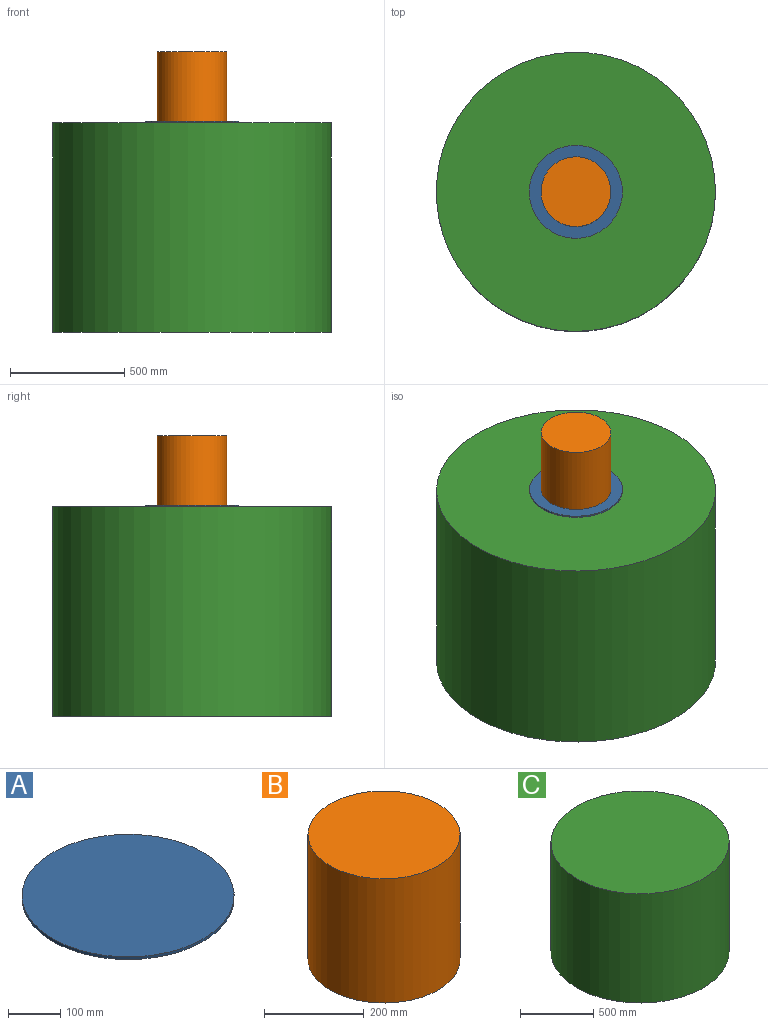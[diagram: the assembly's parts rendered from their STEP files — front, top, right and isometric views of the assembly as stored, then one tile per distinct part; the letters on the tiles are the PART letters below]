
ASSEMBLY  parts=3 mates=2
PART A: 3 faces, bbox 406.4x406.4x6.4 mm
  f0: cylinder r=203.2mm len=406.4mm, axis (0,0,-1), area 8107.3mm2, adj f1,f2
  f1: plane 406.4x406.4mm, normal (0,0,1), area 129717.1mm2, adj f0
  f2: plane 406.4x406.4mm, normal (0,0,-1), area 129717.1mm2, adj f0
PART B: 3 faces, bbox 304.8x304.8x304.8 mm
  f0: cylinder r=152.4mm len=304.8mm, axis (0,0,-1), area 291863.5mm2, adj f1,f2
  f1: plane 304.8x304.8mm, normal (0,0,1), area 72965.9mm2, adj f0
  f2: plane 304.8x304.8mm, normal (0,0,-1), area 72965.9mm2, adj f0
PART C: 3 faces, bbox 1219.2x1219.2x914.4 mm
  f0: cylinder r=609.6mm len=1219.2mm, axis (0,0,1), area 3502362.1mm2, adj f1,f2
  f1: plane 1219.2x1219.2mm, normal (0,0,-1), area 1167454mm2, adj f0
  f2: plane 1219.2x1219.2mm, normal (0,0,1), area 1167454mm2, adj f0
PLACE A t=(-204.63,-101.72,326.25)mm
PLACE B t=(-204.63,-101.72,326.25)mm
PLACE C t=(-204.63,-101.72,326.25)mm fixed
MATE fastened C.f0 <-> A.f0  axis (0,0,1) through (-204.63,-101.72,326.25)mm
MATE fastened B.f0 <-> A.f0  axis (0,0,-1) through (-204.63,-101.72,332.6)mm
